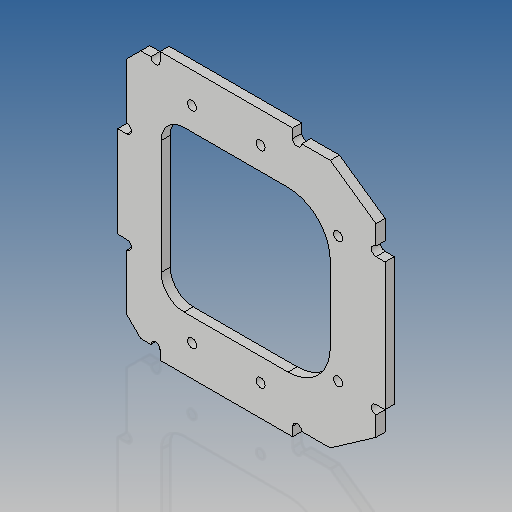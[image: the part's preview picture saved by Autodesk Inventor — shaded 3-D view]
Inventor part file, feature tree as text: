
AUTODESK INVENTOR PART (.ipt)
format: ipt  version: 2017 (Build 210142000, 142)  size: 174,592 bytes
history: native  units: mm
features: reference x9, other x5, extrude x1, sketch x1
ambient origin geometry x8: Origin, YZ Plane, XZ Plane, XY Plane, X Axis, Y Axis, Z Axis, Center Point
bodies: Body1 (feature_tree)
feature tree (16):
  other  "Sólido1"
  extrude  "Extrusión1"  Depth=40.0mm
  sketch  "Boceto1"  dims[d0=109.0mm d1=40.0mm d2=2.0mm d3=109.0mm d7=4.0mm d8=6.0mm d9=6.0mm d10=14.0mm d11=20.0mm d12=14.0mm d13=20.0mm d14=6.0mm d15=6.0mm d16=20.0mm d17=10.0mm d18=4.0mm d19=0.0mm d20=58.0mm d21=3.0mm d22=3.0mm d23=15.0mm d24=4.0mm d26=4.0mm d27=70.0mm]
  reference  "Referencia1"
  reference  "Referencia2"
  reference  "Referencia3"
  reference  "Referencia4"
  reference  "Referencia5"
  reference  "Referencia6"
  reference  "Referencia7"
  reference  "Referencia8"
  reference  "Referencia9"
  other  "<userpath>\Documents\GitHub\actor-re-actor\models\inventor-caja\Case\Case-D.iam"
  other  "Case-D.iam"
  other  "Carcasa:1"
  other  "<userpath>\Documents\GitHub\actor-re-actor\models\inventor-caja\Case\Case-D.iam"
